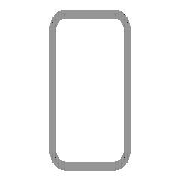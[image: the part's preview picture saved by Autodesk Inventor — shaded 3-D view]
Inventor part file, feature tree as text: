
AUTODESK INVENTOR PART (.ipt)
format: ipt  version: 2025 (Build 290162010, 162A)  size: 133,120 bytes
history: native  units: mm (DEFAULTED — no unit token found)
features: other x4, sketch x1, plane x1
ambient origin geometry x8: Origin, YZ Plane, XZ Plane, XY Plane, X Axis, Y Axis, Z Axis, Center Point
bodies: Solid1 (feature_tree), Body (feature_tree)
feature tree (6):
  parser-record x1  (decoder bookkeeping rows leaked as tree rows — omitted from the tree; the rows remain in map.json)
  other  "Driven Length"
  other  "Start Plane"
  other  "End Plane"
  sketch  "Sketch3"  dims[d3=140.0mm d4=0.0mm d7=6.0mm d9=40.0mm d11=60.0mm d12=3.0mm d13=-0.0mm d14=140.0mm d15=20.0mm d16=30.0mm d17=90.0deg d18=140.0mm]
  plane  "Work Plane3"
